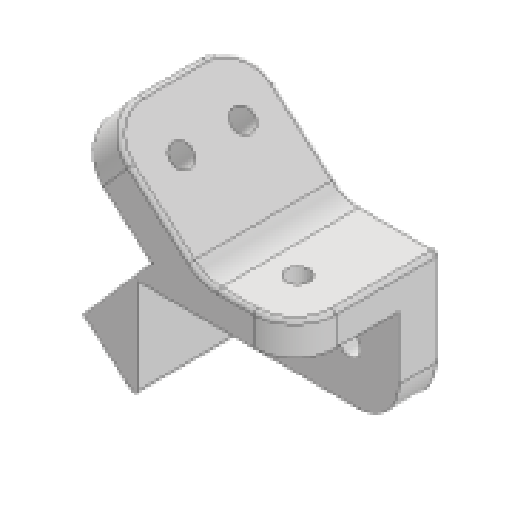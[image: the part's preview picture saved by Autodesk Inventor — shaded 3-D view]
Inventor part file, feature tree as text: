
AUTODESK INVENTOR PART (.ipt)
format: ipt  version: 2025 (Build 290162000, 162)  size: 233,984 bytes
history: native  units: mm
features: extrude x5, sketch x5, reference x4, projected_geometry x3, other x3, fillet x2, mirror x1
ambient origin geometry x8: Origin, YZ Plane, XZ Plane, XY Plane, X Axis, Y Axis, Z Axis, Center Point
bodies: Solid1 (feature_tree)
feature tree (23):
  extrude  "Extrusion1"  Depth=38.1mm
  extrude  "Extrusion2"  Depth=10.0mm TaperAngle=0.0deg
  extrude  "Extrusion3"  Depth=35.4mm TaperAngle=0.0deg
  extrude  "Extrusion5"  Depth=35.4mm TaperAngle=0.0deg
  extrude  "Extrusion6"  TaperAngle=0.0deg  [1 undecoded]
  fillet  "Fillet1"  Radius=10.0mm
  fillet  "Fillet2"  Radius=10.0mm
  mirror  "Mirror1"
  sketch  "Sketch1"  dims[d0=25.4mm d1=38.1mm]
  sketch  "Sketch2"  dims[d2=5.5mm d3=10.0mm d4=0.0mm]
  reference  "Reference1"
  reference  "Reference2"
  reference  "Reference3"
  reference  "Reference4"
  sketch  "Sketch3"  dims[d5=10.0mm d6=35.4mm d7=0.0mm]
  projected_geometry  "Projected Loop1"
  sketch  "Sketch5"  dims[d8=8.0mm d9=35.4mm d10=0.0mm]
  projected_geometry  "Projected Loop3"
  sketch  "Sketch6"  dims[d13=5.5mm d14=0.0mm d15=0.0mm d16=10.0mm d17=0.0mm d18=10.0mm d19=1.0mm]
  projected_geometry  "Projected Loop4"
  other  "<userpath>\Desktop\puppycat\woodhouseMK1.iam"
  other  "woodhouseMK1.iam"
  other  "horizontalStrutLower:1"
note: 1 required parameter value undecoded (feature->parameter linkage not recoverable at this tier; creation-order binding heuristic only, values carry confidence <= 0.55)
